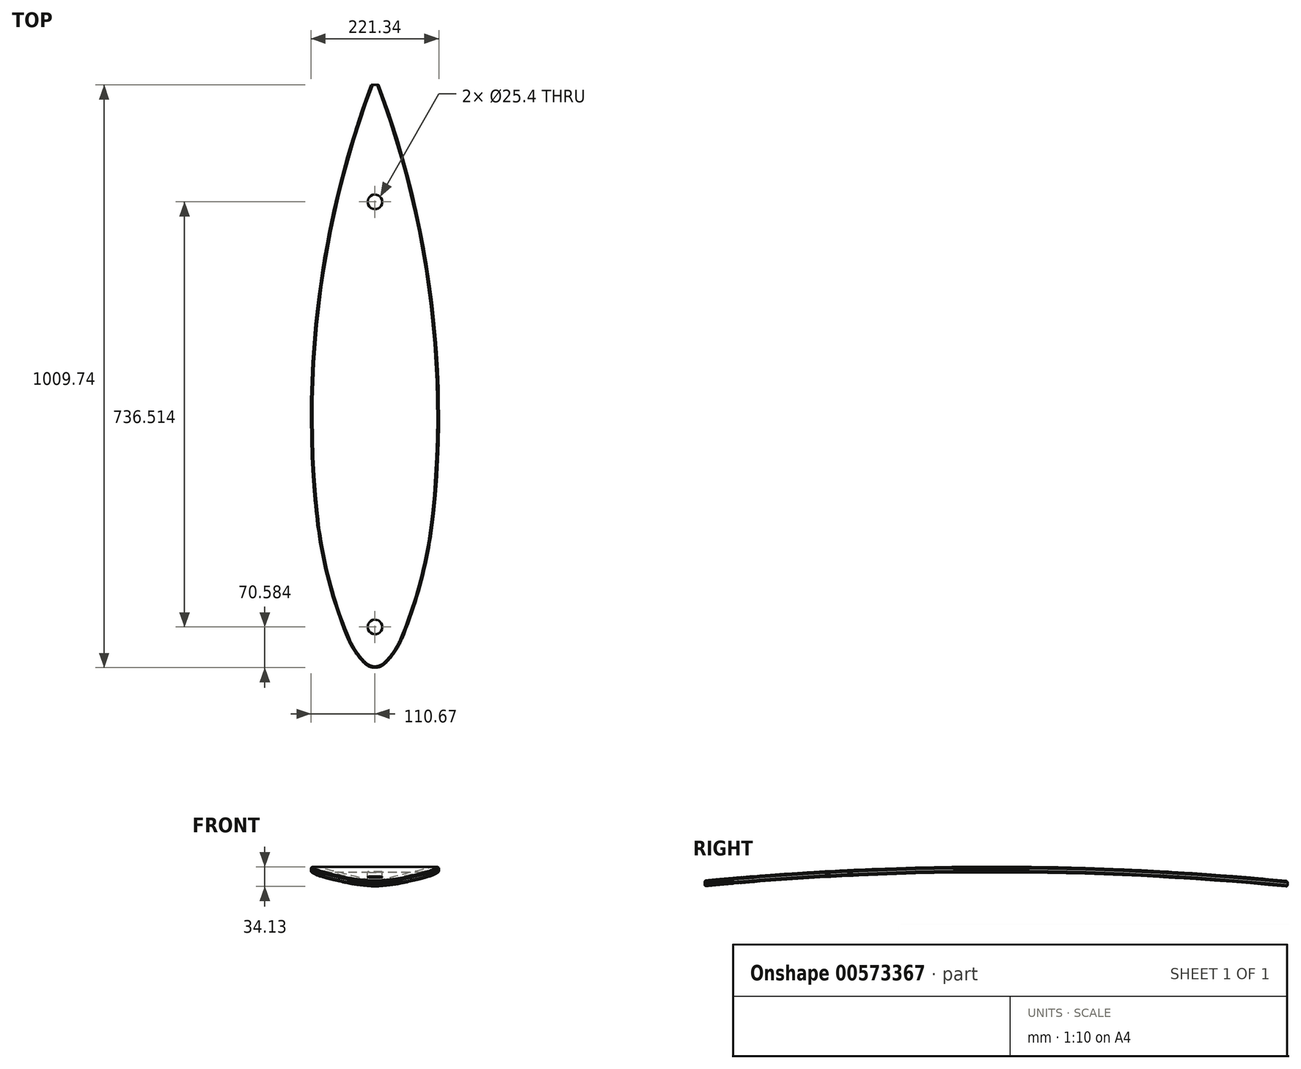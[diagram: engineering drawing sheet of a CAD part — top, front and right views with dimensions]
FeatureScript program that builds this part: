
annotation { "Feature Type Name" : "Feature", "Feature Type Description" : "" }
export const myFeature = defineFeature(function(context is Context, id is Id, definition is map)
    precondition{}
    {
        {
            var Q0;
            Q0=qCreatedBy(makeId("Right.planeOp"),FACE);
            var sketch = newSketch(context, id + "F0", { "sketchPlane" : qUnion([Q0])});
            skLineSegment(sketch, "E0", {"start": v(0, 0) * mm, "end": v(1028.7, 0) * mm, "construction": true});
            skPoint(sketch, "E1", {"position": v(84.13, 12.08) * mm});
            skPoint(sketch, "E2", {"position": v(820.65, 15.05) * mm});
            skArc(sketch, "E3", {"start": v(1028.7, 0) * mm, "mid": v(514.35, 25.4) * mm, "end": v(0, 0) * mm});
            skArc(sketch, "E4.0", {"start": v(1029.64, 9.48) * mm, "mid": v(514.35, 34.93) * mm, "end": v(-0.94, 9.48) * mm});
            skLineSegment(sketch, "E5", {"start": v(-0.94, 9.48) * mm, "end": v(0, 0) * mm});
            skLineSegment(sketch, "E6", {"start": v(1029.64, 9.48) * mm, "end": v(1028.7, 0) * mm});
            skSolve(sketch);
        }
        {
            var Q0;
            Q0 = qSketchRegion(id + "F0", true);
            extrude(context, id + "F1", {"entities" : qUnion([Q0]), "depth" : 114.3 * mm, "offsetDistance" : 25.4 * mm});
        }
        {
            var Q0;
            Q0=qCreatedBy(makeId("Top.planeOp"),FACE);
            var sketch = newSketch(context, id + "F2", { "sketchPlane" : qUnion([Q0])});
            skPoint(sketch, "E7", {"position": v(46.6, 62.69) * mm});
            skPoint(sketch, "E8", {"position": v(101.9, 280.19) * mm});
            skArc(sketch, "E9", {"start": v(101.9, 280.19) * mm, "mid": v(97.34, 657.3) * mm, "end": v(6.35, 1023.29) * mm});
            skArc(sketch, "E10", {"start": v(46.6, 62.69) * mm, "mid": v(82.22, 169.41) * mm, "end": v(101.9, 280.19) * mm});
            skArc(sketch, "E11", {"start": v(0, 6.35) * mm, "mid": v(27.34, 31.18) * mm, "end": v(46.6, 62.69) * mm});
            skPoint(sketch, "E12", {"position": v(6.35, 1023.29) * mm});
            skLineSegment(sketch, "E13", {"start": v(6.35, 1023.29) * mm, "end": v(0, 1023.29) * mm});
            skLineSegment(sketch, "E14", {"start": v(0, 1023.29) * mm, "end": v(0, 1029.64) * mm});
            skLineSegment(sketch, "E15", {"start": v(0, 1029.64) * mm, "end": v(114.3, 1029.64) * mm});
            skLineSegment(sketch, "E16", {"start": v(114.3, 1029.64) * mm, "end": v(114.3, 0) * mm});
            skLineSegment(sketch, "E17", {"start": v(114.3, 0) * mm, "end": v(0, 0) * mm});
            skLineSegment(sketch, "E18", {"start": v(0, 6.35) * mm, "end": v(0, 0) * mm});
            skSolve(sketch);
        }
        {
            var Q0;
            Q0 = qSketchRegion(id + "F2", true);
            extrude(context, id + "F3", {"entities" : qUnion([Q0]), "operationType" : NewBodyOperationType.REMOVE, "endBound" : BoundingType.SYMMETRIC, "depth" : 127 * mm, "offsetDistance" : 25.4 * mm});
        }
        {
            var Q0;
            Q0=makeQuery(id+"F1.opExtrude","SWEPT_FACE",FACE,{"disambiguationData":[OSD([sQuery(id+"F0.wireOp",EDGE,"E5")])]});
            extrude(context, id + "F4", {"entities" : qUnion([Q0]), "operationType" : NewBodyOperationType.REMOVE, "endBound" : BoundingType.SYMMETRIC, "depth" : 7.62 * mm, "offsetDistance" : 25.4 * mm});
        }
        {
            var Q0;
            Q0=makeQuery(id+"F3.boolean.opBoolean","SPLIT",BODY,{"disambiguationData":[OD(1.0)],"derivedFrom":makeQuery(id+"F1.opExtrude","SWEPT_BODY",BODY,{"disambiguationData":[OSD([sQuery(id+"F0.wireOp",EDGE,"E3"),sQuery(id+"F0.wireOp",EDGE,"E4.0"),sQuery(id+"F0.wireOp",EDGE,"E5"),sQuery(id+"F0.wireOp",EDGE,"E6")])]})});
            var Q1;
            {var subQ0=sQuery(id+"F0.wireOp",EDGE,"E3");var subQ1=sQuery(id+"F0.wireOp",EDGE,"E4.0");Q1=makeQuery(id+"F3.boolean.opBoolean","SPLIT",FACE,{"disambiguationData":[TD([makeQuery(id+"F1.opExtrude","SWEPT_FACE",FACE,{"disambiguationData":[OSD([subQ0])]})])],"derivedFrom":makeQuery(id+"F1.opExtrude","CAP_FACE",FACE,{"disambiguationData":[OSD([subQ0,subQ1,sQuery(id+"F0.wireOp",EDGE,"E5"),sQuery(id+"F0.wireOp",EDGE,"E6")])],"isStart":true})});}
            mirror(context, id + "F5", {"operationType" : NewBodyOperationType.ADD, "entities" : qUnion([Q0]), "mirrorPlane" : qUnion([Q1])});
        }
        {
            var Q0;
            {var subQ0=makeQuery(id+"F3.boolean.opBoolean","COPY",EDGE,{"derivedFrom":makeQuery(id+"F3.opExtrude","SWEPT_EDGE",EDGE,{"disambiguationData":[OSD([sQuery(id+"F2.wireOp",EDGE,"E11"),sQuery(id+"F2.wireOp",EDGE,"E18")])]})});Q0=makeQuery(id+"F5.boolean.opBoolean","MERGE",EDGE,{"derivedFrom":[subQ0,makeQuery(id+"F5.opPattern","COPY",EDGE,{"derivedFrom":subQ0,"instanceName":"1"})]});}
            fillet(context, id + "F6", {"entities" : qUnion([Q0]), "radius" : 25.4 * mm, "tangentPropagation" : true, "allowEdgeOverflow" : false});
        }
        {
            var Q0;
            {var subQ0=makeQuery(id+"F1.opExtrude","SWEPT_FACE",FACE,{"disambiguationData":[OSD([sQuery(id+"F0.wireOp",EDGE,"E3")])]});Q0=makeQuery(id+"F5.boolean.opBoolean","MERGE",FACE,{"derivedFrom":[subQ0,makeQuery(id+"F5.opPattern","COPY",FACE,{"derivedFrom":subQ0,"instanceName":"1"})]});}
            var Q1;
            {var subQ0=sQuery(id+"F0.wireOp",EDGE,"E4.0");var subQ1=makeQuery(id+"F3.boolean.opBoolean","SPLIT",FACE,{"disambiguationData":[TD([makeQuery(id+"F3.opExtrude","SWEPT_FACE",FACE,{"disambiguationData":[OSD([sQuery(id+"F2.wireOp",EDGE,"E9")])]})])],"derivedFrom":makeQuery(id+"F1.opExtrude","SWEPT_FACE",FACE,{"disambiguationData":[OSD([subQ0])]})});Q1=makeQuery(id+"F5.boolean.opBoolean","MERGE",FACE,{"derivedFrom":[subQ1,makeQuery(id+"F5.opPattern","COPY",FACE,{"derivedFrom":subQ1,"instanceName":"1"})]});}
            fillet(context, id + "F7", {"entities" : qUnion([Q0, Q1]), "radius" : 2.54 * mm, "tangentPropagation" : true, "allowEdgeOverflow" : false});
        }
        {
            var Q0;
            Q0=qCreatedBy(makeId("Top.planeOp"),FACE);
            var sketch = newSketch(context, id + "F8", { "sketchPlane" : qUnion([Q0])});
            skCircle(sketch, "E19", {"center": v(0, 84.13) * mm, "radius": 12.7 * mm});
            skCircle(sketch, "E20", {"center": v(0, 820.65) * mm, "radius": 12.7 * mm});
            skSolve(sketch);
        }
        {
            var Q0;
            Q0 = qSketchRegion(id + "F8", true);
            extrude(context, id + "F9", {"entities" : qUnion([Q0]), "operationType" : NewBodyOperationType.REMOVE, "endBound" : BoundingType.SYMMETRIC, "oppositeDirection" : true, "depth" : 152.4 * mm, "offsetDistance" : 25.4 * mm});
        }
        {
            var Q0;
            Q0=qCreatedBy(makeId("Top.planeOp"),FACE);
            var sketch = newSketch(context, id + "F10", { "sketchPlane" : qUnion([Q0])});
            skLineSegment(sketch, "E21", {"start": v(0, 7.02) * mm, "end": v(0, 84.13) * mm, "construction": true});
            skSolve(sketch);
        }
        {
            var Q0;
            Q0=qCreatedBy(makeId("Right.planeOp"),FACE);
            var sketch = newSketch(context, id + "F11", { "sketchPlane" : qUnion([Q0])});
            skLineSegment(sketch, "E22", {"start": v(84.13, 0) * mm, "end": v(84.13, 16.35) * mm, "construction": true});
            skSolve(sketch);
        }
        {
            var Q0;
            Q0=qCreatedBy(makeId("Top.planeOp"),FACE);
            var sketch = newSketch(context, id + "F12", { "sketchPlane" : qUnion([Q0])});
            skLineSegment(sketch, "E23", {"start": v(0, 1023.29) * mm, "end": v(0, 820.65) * mm});
            skSolve(sketch);
        }
        {
            var Q0;
            Q0=qCreatedBy(makeId("Right.planeOp"),FACE);
            var sketch = newSketch(context, id + "F13", { "sketchPlane" : qUnion([Q0])});
            skLineSegment(sketch, "E24", {"start": v(820.65, 0) * mm, "end": v(820.65, 25.8) * mm});
            skSolve(sketch);
        }
    });
